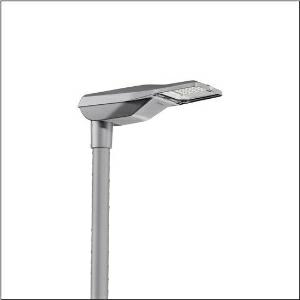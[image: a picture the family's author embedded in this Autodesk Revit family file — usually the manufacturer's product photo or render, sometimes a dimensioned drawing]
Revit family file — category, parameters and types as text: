
# Revit family: streetlight_sl_21_micro___stw1_0a_5xe5e43a08db_fcac
name_source: partatom
category: Lighting Fixtures
units: mm (PartAtom-declared; Revit-internal decimal feet)

## family parameters
Cut with Voids When Loaded = No
Host = Face
Light Source = No
Part Type = Normal
Room Calculation Point = No
Round Connector Dimension = Use Diameter
Shared = No

## types (1)
- --- (1 x LED, 5320 lm, 39.1 W, 4000K)
    Apparent Load = 39 VA
    CIE Flux Codes = 38 75 98 100 100
    Color Rendering = 70
    Color Temperature = 4000K
    Default Elevation = 1800 mm
    Description = Streetlight SL 21 micro, mast luminaire, primary light control with lens, of PMMA, primary optical cover: cover, of toughened safety glass, transparent, light distribution: STW1.0a, light emission: direct distribution, primary light characteristic: asymmetric, installation type: side-entry, post-top, LED, 3G 1.5mm², High Power LED, rated luminous flux: 5.320lm, luminous efficacy: 136lm/W, light colour: 740, colour temperature: 4000K, control gear: Easy, control: flexible luminous flux parameterisation, time-dependent luminous flux control, constant luminous flux control, overheat protection, mains connection: 230..240V, AC, 50/60Hz, connection cable pre-assembled, cable length: 6,5m, wiring characteristics: H07RN-F, start of lifetime: 39W, end of service life: 41W, reduction: 18W, luminaire housing, of diecast aluminium, powder-coated, Siteco® metallic grey (DB 702S), corrosivity category C5 mid according to DIN EN ISO 12944, please order mast flange separately, inclination adjustable: 0°, 5°, 10°, 15°, sealing non-destructively replaceable, multi-level sealing system, length: 528mm, width: 235mm, height: 110mm, mast flange for spigot size: 42mm (side-entry): 5XC10008XM4, 60/48mm (side-entry/post-top): 5XC10108XM2, 76/60mm (side-entry/post-top): 5XC10108XM1, protection rating (complete): IP66, insulation class (complete): insulation class II (safety insulation), certification: CE, ENEC, ENEC+, VDE, impact resistance: IK10, permissible operating ambient temperature for outdoor applications: -40..+50°C, standard-compliant lighting for roads and squares, packaging unit: 1 piece

Light Distribution: STW1.0a
    Height = 110 mm
    Lamp = 1 x LED
    Lamp Light Flux = 5320 lm
    Lamp Power = 39.1 W
    Lamp count = 1
    Length = 528 mm
    Luminous efficacy = 136 lm/W
    Manufacturer = Siteco
    ModVariant = No
    Model = 5XE5E43A08DB
    Number of Poles = 1
    OnlyDefault = Yes
    Power Factor = 1
    Product Name = Streetlight SL 21 micro | STW1.0a
    Product group = mast luminaire | pylon top
    ProductGroupID = 6100
    Protection Class = Protection class II
    Protection Degree = IP 66
    RLX_Detail_Level = 1
    RLX_Emergency_Light_Flux = 0 lm
    RLX_Emergency_Type = 0
    RLX_Emergency_Type_DB = No
    RlxData = <blob elided: 99533 chars, md5=6caff91b>
    Socket = socket
    Standby Power = 0 W
    System Light Flux = 5320 lm
    System Power = 39 W
    Type Comments = factory setting: luminous flux: 100 % | Output Level: 100 % | 765 mA
    Type Image = l_1006881.jpg
    URL = http://relux.com
    VarID = @adj_176557
    Voltage = 0 V
    Weight = 0.00 kg
    Width = 235 mm

## geometry (parser evidence)
native form markers: Blend x4, Sweep x11
no freeform markers — native parametric forms only
